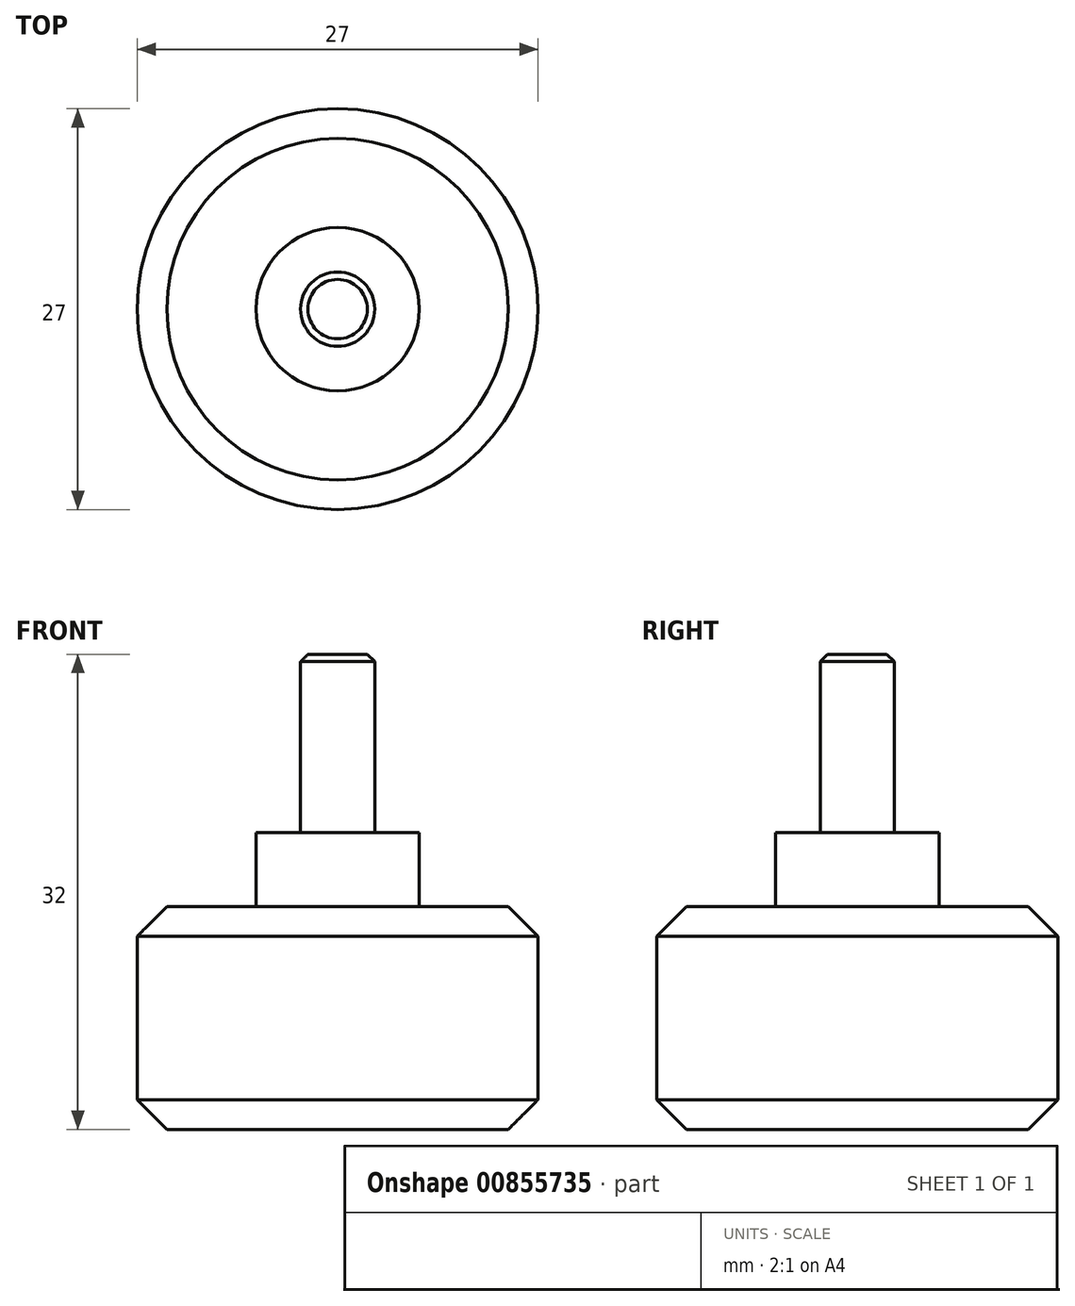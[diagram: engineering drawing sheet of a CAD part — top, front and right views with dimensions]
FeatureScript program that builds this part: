
annotation { "Feature Type Name" : "Feature", "Feature Type Description" : "" }
export const myFeature = defineFeature(function(context is Context, id is Id, definition is map)
    precondition{}
    {
        {
            var Q0;
            Q0=qCreatedBy(makeId("Front.planeOp"),FACE);
            var sketch = newSketch(context, id + "F0", { "sketchPlane" : qUnion([Q0])});
            skLineSegment(sketch, "E0", {"start": v(0, 0) * mm, "end": v(13.5, 0) * mm});
            skLineSegment(sketch, "E1", {"start": v(13.5, 15) * mm, "end": v(5.5, 15) * mm});
            skLineSegment(sketch, "E2", {"start": v(5.5, 15) * mm, "end": v(5.5, 20) * mm});
            skLineSegment(sketch, "E3", {"start": v(5.5, 20) * mm, "end": v(2.5, 20) * mm});
            skLineSegment(sketch, "E4", {"start": v(2.5, 20) * mm, "end": v(2.5, 32) * mm});
            skLineSegment(sketch, "E5", {"start": v(2.5, 32) * mm, "end": v(0, 32) * mm});
            skLineSegment(sketch, "E6", {"start": v(0, 32) * mm, "end": v(0, 0) * mm});
            skLineSegment(sketch, "E7.trimOffspring", {"start": v(13.5, 0) * mm, "end": v(13.5, 15) * mm});
            skSolve(sketch);
        }
        {
            var Q0;
            Q0=qSketchRegion(id+"F0",true);
            var Q1;
            Q1=sQuery(id+"F0.wireOp",EDGE,"E6");
            revolve(context, id + "F1", {"surfaceOperationType" : NewSurfaceOperationType.NEW, "entities" : qUnion([Q0]), "axis" : qUnion([Q1]), "revolveType" : RevolveType.FULL});
        }
        {
            var Q0;
            Q0=makeQuery(id+"F1.opRevolve","SWEPT_EDGE",EDGE,{"disambiguationData":[OSD([sQuery(id+"F0.wireOp",EDGE,"E1"),sQuery(id+"F0.wireOp",EDGE,"E7.trimOffspring")])]});
            var Q1;
            Q1=makeQuery(id+"F1.opRevolve","SWEPT_EDGE",EDGE,{"disambiguationData":[OSD([sQuery(id+"F0.wireOp",EDGE,"E0"),sQuery(id+"F0.wireOp",EDGE,"gGLPZcZM-4izV-Hhaf-EASS-Gusj4DygHxA4")])]});
            chamfer(context, id + "F2", {"entities" : qUnion([Q0, Q1]), "width" : 2 * mm, "tangentPropagation" : true});
        }
        {
            var Q0;
            Q0=makeQuery(id+"F1.opRevolve","SWEPT_EDGE",EDGE,{"disambiguationData":[OSD([sQuery(id+"F0.wireOp",EDGE,"E4"),sQuery(id+"F0.wireOp",EDGE,"E5")])]});
            chamfer(context, id + "F3", {"entities" : qUnion([Q0]), "width" : 0.5 * mm, "tangentPropagation" : true});
        }
    });
